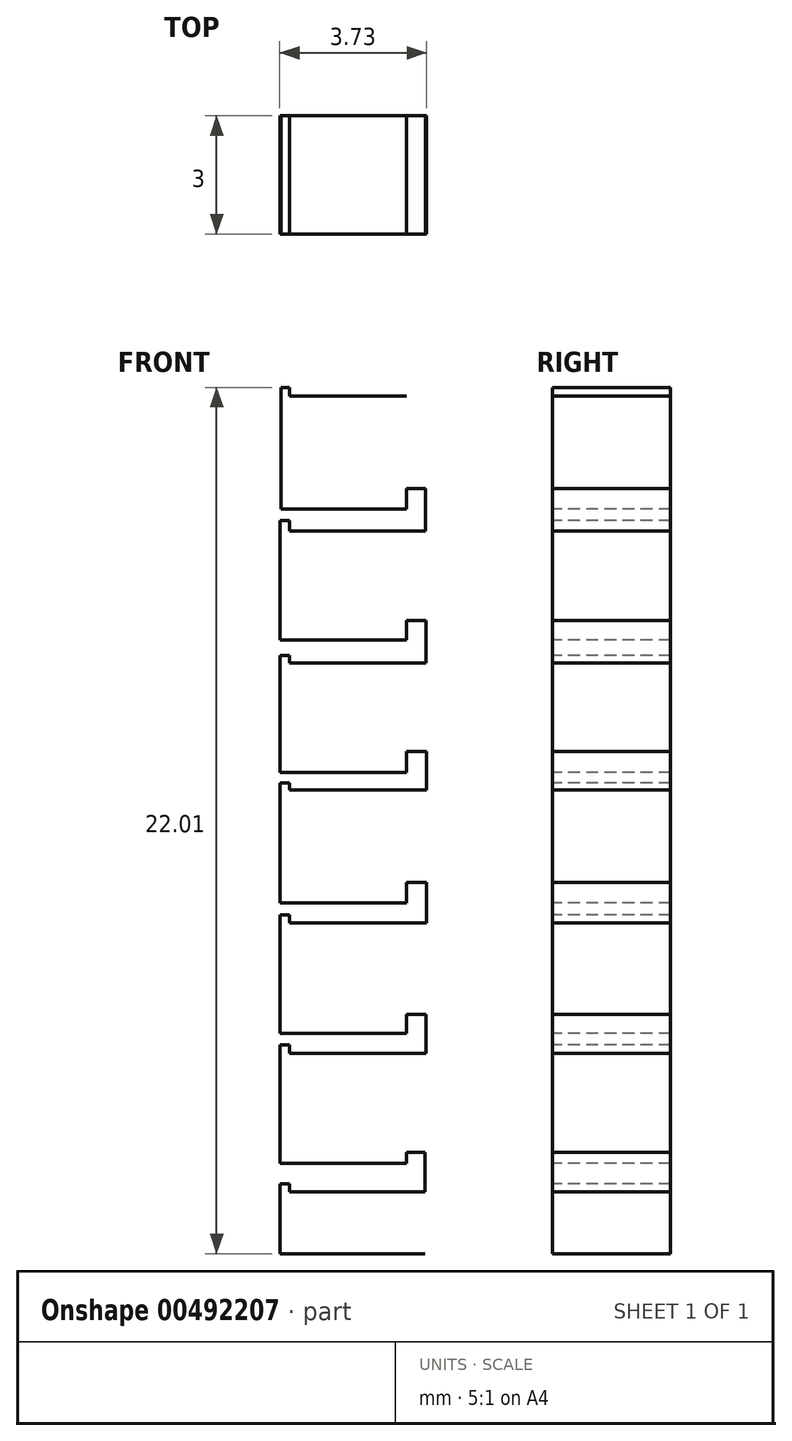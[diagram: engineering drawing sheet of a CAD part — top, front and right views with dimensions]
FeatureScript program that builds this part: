
annotation { "Feature Type Name" : "Feature", "Feature Type Description" : "" }
export const myFeature = defineFeature(function(context is Context, id is Id, definition is map)
    precondition{}
    {
        {
            var Q0;
            Q0=qCreatedBy(makeId("Front.planeOp"),FACE);
            var sketch = newSketch(context, id + "F0", { "sketchPlane" : qUnion([Q0])});
            skLineSegment(sketch, "E0", {"start": v(-53.72, 66.5) * mm, "end": v(-50.52, 66.5) * mm});
            skLineSegment(sketch, "E1", {"start": v(-50.52, 66.5) * mm, "end": v(-50.52, 67.02) * mm});
            skLineSegment(sketch, "E2", {"start": v(-50.52, 67.02) * mm, "end": v(-50.05, 67.02) * mm});
            skLineSegment(sketch, "E3", {"start": v(-50.05, 67.02) * mm, "end": v(-50.05, 65.94) * mm});
            skLineSegment(sketch, "E4", {"start": v(-50.05, 65.94) * mm, "end": v(-53.5, 65.94) * mm});
            skLineSegment(sketch, "E5", {"start": v(-53.5, 65.94) * mm, "end": v(-53.5, 66.2) * mm});
            skLineSegment(sketch, "E6", {"start": v(-53.5, 66.2) * mm, "end": v(-53.74, 66.2) * mm});
            skLineSegment(sketch, "E7", {"start": v(-53.74, 66.2) * mm, "end": v(-53.74, 63.17) * mm});
            skLineSegment(sketch, "E8", {"start": v(-53.74, 63.17) * mm, "end": v(-50.52, 63.17) * mm});
            skLineSegment(sketch, "E9", {"start": v(-50.52, 63.17) * mm, "end": v(-50.52, 63.67) * mm});
            skLineSegment(sketch, "E10", {"start": v(-50.52, 63.67) * mm, "end": v(-50.04, 63.67) * mm});
            skLineSegment(sketch, "E11", {"start": v(-50.04, 63.67) * mm, "end": v(-50.04, 62.59) * mm});
            skLineSegment(sketch, "E12", {"start": v(-50.04, 62.59) * mm, "end": v(-53.5, 62.59) * mm});
            skLineSegment(sketch, "E13", {"start": v(-53.5, 62.59) * mm, "end": v(-53.5, 62.78) * mm});
            skLineSegment(sketch, "E14", {"start": v(-53.5, 62.78) * mm, "end": v(-53.75, 62.78) * mm});
            skLineSegment(sketch, "E15", {"start": v(-53.75, 62.78) * mm, "end": v(-53.75, 59.8) * mm});
            skLineSegment(sketch, "E16", {"start": v(-53.75, 59.8) * mm, "end": v(-50.52, 59.8) * mm});
            skLineSegment(sketch, "E17", {"start": v(-50.52, 59.8) * mm, "end": v(-50.52, 60.33) * mm});
            skLineSegment(sketch, "E18", {"start": v(-50.52, 60.33) * mm, "end": v(-50.02, 60.33) * mm});
            skLineSegment(sketch, "E19", {"start": v(-50.02, 60.33) * mm, "end": v(-50.02, 59.36) * mm});
            skLineSegment(sketch, "E20", {"start": v(-50.02, 59.36) * mm, "end": v(-53.5, 59.36) * mm});
            skLineSegment(sketch, "E21", {"start": v(-53.5, 59.36) * mm, "end": v(-53.5, 59.55) * mm});
            skLineSegment(sketch, "E22", {"start": v(-53.5, 59.55) * mm, "end": v(-53.75, 59.55) * mm});
            skLineSegment(sketch, "E23", {"start": v(-53.75, 59.55) * mm, "end": v(-53.75, 56.5) * mm});
            skLineSegment(sketch, "E24", {"start": v(-53.75, 56.5) * mm, "end": v(-50.52, 56.5) * mm});
            skLineSegment(sketch, "E25", {"start": v(-50.52, 56.5) * mm, "end": v(-50.52, 57.01) * mm});
            skLineSegment(sketch, "E26", {"start": v(-50.52, 57.01) * mm, "end": v(-50.02, 57.01) * mm});
            skLineSegment(sketch, "E27", {"start": v(-50.02, 57.01) * mm, "end": v(-50.02, 55.98) * mm});
            skLineSegment(sketch, "E28", {"start": v(-50.02, 55.98) * mm, "end": v(-53.5, 55.98) * mm});
            skLineSegment(sketch, "E29", {"start": v(-53.5, 55.98) * mm, "end": v(-53.5, 56.18) * mm});
            skLineSegment(sketch, "E30", {"start": v(-53.5, 56.18) * mm, "end": v(-53.75, 56.18) * mm});
            skLineSegment(sketch, "E31", {"start": v(-53.72, 66.5) * mm, "end": v(-53.72, 69.6) * mm});
            skLineSegment(sketch, "E32", {"start": v(-53.72, 69.6) * mm, "end": v(-53.5, 69.6) * mm});
            skLineSegment(sketch, "E33", {"start": v(-53.5, 69.6) * mm, "end": v(-53.5, 69.37) * mm});
            skLineSegment(sketch, "E34", {"start": v(-53.5, 69.37) * mm, "end": v(-50.52, 69.37) * mm});
            skLineSegment(sketch, "E35", {"start": v(-53.75, 56.18) * mm, "end": v(-53.75, 53.17) * mm});
            skLineSegment(sketch, "E36", {"start": v(-53.75, 53.17) * mm, "end": v(-50.52, 53.17) * mm});
            skLineSegment(sketch, "E37", {"start": v(-50.52, 53.17) * mm, "end": v(-50.52, 53.67) * mm});
            skLineSegment(sketch, "E38", {"start": v(-50.52, 53.67) * mm, "end": v(-50.03, 53.67) * mm});
            skLineSegment(sketch, "E39", {"start": v(-50.03, 53.67) * mm, "end": v(-50.03, 52.67) * mm});
            skLineSegment(sketch, "E40", {"start": v(-50.03, 52.67) * mm, "end": v(-53.5, 52.67) * mm});
            skLineSegment(sketch, "E41", {"start": v(-53.5, 52.67) * mm, "end": v(-53.5, 52.88) * mm});
            skLineSegment(sketch, "E42", {"start": v(-53.5, 52.88) * mm, "end": v(-53.75, 52.88) * mm});
            skLineSegment(sketch, "E43", {"start": v(-53.75, 52.88) * mm, "end": v(-53.75, 49.88) * mm});
            skPoint(sketch, "E43.endSnap0", {"position": v(-53.75, 54.68) * mm});
            skLineSegment(sketch, "E44", {"start": v(-53.75, 49.88) * mm, "end": v(-50.52, 49.88) * mm});
            skLineSegment(sketch, "E45", {"start": v(-50.52, 49.88) * mm, "end": v(-50.52, 50.16) * mm});
            skLineSegment(sketch, "E46", {"start": v(-50.52, 50.16) * mm, "end": v(-50.06, 50.16) * mm});
            skLineSegment(sketch, "E47", {"start": v(-50.06, 50.16) * mm, "end": v(-50.06, 49.15) * mm});
            skLineSegment(sketch, "E48", {"start": v(-50.06, 49.15) * mm, "end": v(-53.5, 49.15) * mm});
            skLineSegment(sketch, "E49", {"start": v(-53.5, 49.15) * mm, "end": v(-53.5, 49.35) * mm});
            skLineSegment(sketch, "E50", {"start": v(-53.5, 49.35) * mm, "end": v(-53.75, 49.35) * mm});
            skLineSegment(sketch, "E51", {"start": v(-53.75, 49.35) * mm, "end": v(-53.75, 47.58) * mm});
            skLineSegment(sketch, "E52", {"start": v(-53.75, 47.58) * mm, "end": v(-50.06, 47.58) * mm});
            skSolve(sketch);
        }
        {
            var Q0;
            Q0=sQuery(id+"F0.wireOp",EDGE,"E12");
            var Q1;
            Q1=sQuery(id+"F0.wireOp",EDGE,"E8");
            var Q2;
            Q2=sQuery(id+"F0.wireOp",EDGE,"E43");
            var Q3;
            Q3=sQuery(id+"F0.wireOp",EDGE,"E23");
            var Q4;
            Q4=sQuery(id+"F0.wireOp",EDGE,"E48");
            var Q5;
            Q5=sQuery(id+"F0.wireOp",EDGE,"E7");
            var Q6;
            Q6=sQuery(id+"F0.wireOp",EDGE,"E20");
            var Q7;
            Q7=sQuery(id+"F0.wireOp",EDGE,"E52");
            var Q8;
            Q8=sQuery(id+"F0.wireOp",EDGE,"E16");
            var Q9;
            Q9=sQuery(id+"F0.wireOp",EDGE,"E36");
            var Q10;
            Q10=sQuery(id+"F0.wireOp",EDGE,"E15");
            var Q11;
            Q11=sQuery(id+"F0.wireOp",EDGE,"E31");
            var Q12;
            Q12=sQuery(id+"F0.wireOp",EDGE,"E0");
            var Q13;
            Q13=sQuery(id+"F0.wireOp",EDGE,"E4");
            var Q14;
            Q14=sQuery(id+"F0.wireOp",EDGE,"E40");
            var Q15;
            Q15=sQuery(id+"F0.wireOp",EDGE,"E24");
            var Q16;
            Q16=sQuery(id+"F0.wireOp",EDGE,"E28");
            var Q17;
            Q17=sQuery(id+"F0.wireOp",EDGE,"E44");
            var Q18;
            Q18=sQuery(id+"F0.wireOp",EDGE,"E35");
            var Q19;
            Q19=sQuery(id+"F0.wireOp",EDGE,"E34");
            var Q20;
            Q20=sQuery(id+"F0.wireOp",EDGE,"E51");
            var Q21;
            Q21=sQuery(id+"F0.wireOp",EDGE,"E11");
            var Q22;
            Q22=sQuery(id+"F0.wireOp",EDGE,"E32");
            var Q23;
            Q23=sQuery(id+"F0.wireOp",EDGE,"E9");
            var Q24;
            Q24=sQuery(id+"F0.wireOp",EDGE,"E10");
            var Q25;
            Q25=sQuery(id+"F0.wireOp",EDGE,"E39");
            var Q26;
            Q26=sQuery(id+"F0.wireOp",EDGE,"E27");
            var Q27;
            Q27=sQuery(id+"F0.wireOp",EDGE,"E26");
            var Q28;
            Q28=sQuery(id+"F0.wireOp",EDGE,"E30");
            var Q29;
            Q29=sQuery(id+"F0.wireOp",EDGE,"E17");
            var Q30;
            Q30=sQuery(id+"F0.wireOp",EDGE,"E42");
            var Q31;
            Q31=sQuery(id+"F0.wireOp",EDGE,"E45");
            var Q32;
            Q32=sQuery(id+"F0.wireOp",EDGE,"E46");
            var Q33;
            Q33=sQuery(id+"F0.wireOp",EDGE,"E1");
            var Q34;
            Q34=sQuery(id+"F0.wireOp",EDGE,"E29");
            var Q35;
            Q35=sQuery(id+"F0.wireOp",EDGE,"E47");
            var Q36;
            Q36=sQuery(id+"F0.wireOp",EDGE,"E37");
            var Q37;
            Q37=sQuery(id+"F0.wireOp",EDGE,"E25");
            var Q38;
            Q38=sQuery(id+"F0.wireOp",EDGE,"E41");
            var Q39;
            Q39=sQuery(id+"F0.wireOp",EDGE,"E6");
            var Q40;
            Q40=sQuery(id+"F0.wireOp",EDGE,"E22");
            var Q41;
            Q41=sQuery(id+"F0.wireOp",EDGE,"E5");
            var Q42;
            Q42=sQuery(id+"F0.wireOp",EDGE,"E38");
            var Q43;
            Q43=sQuery(id+"F0.wireOp",EDGE,"E18");
            var Q44;
            Q44=sQuery(id+"F0.wireOp",EDGE,"E33");
            var Q45;
            Q45=sQuery(id+"F0.wireOp",EDGE,"E3");
            var Q46;
            Q46=sQuery(id+"F0.wireOp",EDGE,"E49");
            var Q47;
            Q47=sQuery(id+"F0.wireOp",EDGE,"E2");
            var Q48;
            Q48=sQuery(id+"F0.wireOp",EDGE,"E14");
            var Q49;
            Q49=sQuery(id+"F0.wireOp",EDGE,"E50");
            var Q50;
            Q50=sQuery(id+"F0.wireOp",EDGE,"E13");
            var Q51;
            Q51=sQuery(id+"F0.wireOp",EDGE,"E19");
            var Q52;
            Q52=sQuery(id+"F0.wireOp",EDGE,"E21");
            extrude(context, id + "F1", {"bodyType" : ToolBodyType.SURFACE, "surfaceEntities" : qUnion([Q0, Q1, Q2, Q3, Q4, Q5, Q6, Q7, Q8, Q9, Q10, Q11, Q12, Q13, Q14, Q15, Q16, Q17, Q18, Q19, Q20, Q21, Q22, Q23, Q24, Q25, Q26, Q27, Q28, Q29, Q30, Q31, Q32, Q33, Q34, Q35, Q36, Q37, Q38, Q39, Q40, Q41, Q42, Q43, Q44, Q45, Q46, Q47, Q48, Q49, Q50, Q51, Q52]), "depth" : 3 * mm});
        }
    });
